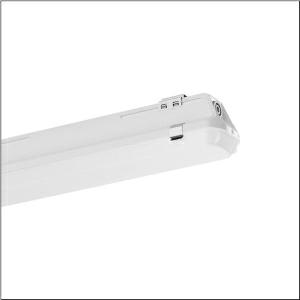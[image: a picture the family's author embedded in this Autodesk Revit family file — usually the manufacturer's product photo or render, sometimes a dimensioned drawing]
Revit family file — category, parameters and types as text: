
# Revit family: monsun_r__11_51fp20fp460h_df5a
name_source: partatom
category: Lighting Fixtures
units: mm (PartAtom-declared; Revit-internal decimal feet)

## family parameters
Cut with Voids When Loaded = No
Host = Face
Light Source = No
Part Type = Normal
Room Calculation Point = No
Round Connector Dimension = Use Diameter
Shared = No

## types (1)
- --- (1 x LED, 5450 lm, 34.6 W, 4000K)
    Apparent Load = 35 VA
    CIE Flux Codes = 45 75 93 94 100
    Color Rendering = 80
    Color Temperature = 4000K
    Default Elevation = 1800 mm
    Description = Monsun® 11, damp-proof luminaire, chain hanger, primary optical cover: enclosure, of PC, light emission: direct distribution, primary light characteristic: symmetric, installation type: suspended mounting, surface-mounted, horizontal mounting, vertical mounting, LED, rated luminous flux: 5.450lm, luminous efficacy: 158lm/W, light colour: 840, colour temperature: 4000K, control gear: ECG DALI, with terminal, 5-pole, max. 2.5mm², mains connection: 220..240V, AC, 50/60Hz, start of lifetime: 35W, end of service life: 39W, luminaire housing, of glass-fibre reinforced polyester, uncoated, bright grey, incl. chain hanger, length: 1.590mm, width: 90mm, height: 88mm, clip for enclosure, of stainless steel (V2A), ceiling mounting element, of stainless steel (V2A), chain hanger, of stainless steel (V2A), protection rating (complete): IP66, insulation class (complete): insulation class I (protective earthing), certification: CE, ENEC, VDE, UKCA, protection symbol: D, impact resistance: IK08, permissible operating ambient temperature: -25..+40°C, standard: EN 50419, EN 60598-2-1, no direct snow, no direct sun, no direct rain, for indoor or canopied outdoor use, corresponds to IFS (International Featured Standards) requirements for safety and quality in the food industry, contact your sales advisor before using the luminaires in applications with unclear chemical exposure, large temperature fluctuations or condensation-forming humidity, LABS conformity tested according to VDMA 24364:2018-05, packaging unit: 1 piece
    Height = 89 mm
    Lamp = 1 x LED
    Lamp Light Flux = 5450 lm
    Lamp Power = 34.6 W
    Lamp count = 1
    Length = 1590 mm
    Luminous efficacy = 158 lm/W
    Manufacturer = Siteco
    ModVariant = No
    Model = 51FP20FP460H
    Mounting Place = Ceiling
    Mounting Type = Surface mounted
    Number of Poles = 1
    OnlyDefault = Yes
    Power Factor = 1
    Product Name = Monsun® 11
    Product group = damp-proof luminaire
    ProductGroupID = 300
    Protection Class = Protection class I
    Protection Degree = IP 66
    RLX_Detail_Level = 1
    RLX_Emergency_Light_Flux = 0 lm
    RLX_Emergency_Type = 0
    RLX_Emergency_Type_DB = No
    RlxData = <blob elided: 92905 chars, md5=d0775e80>
    Socket = socket
    Standby Power = 0 W
    System Light Flux = 5450 lm
    System Power = 35 W
    Type Comments = factory setting: luminous flux: 100 % | dim-lin: 254 | 232 mA
    Type Image = l_1004748.jpg
    URL = http://relux.com
    VarID = @adj_140419
    Voltage = 0 V
    Weight = 0.00 kg
    Width = 90 mm

## geometry (parser evidence)
native form markers: Blend x4, Sweep x12
no freeform markers — native parametric forms only
